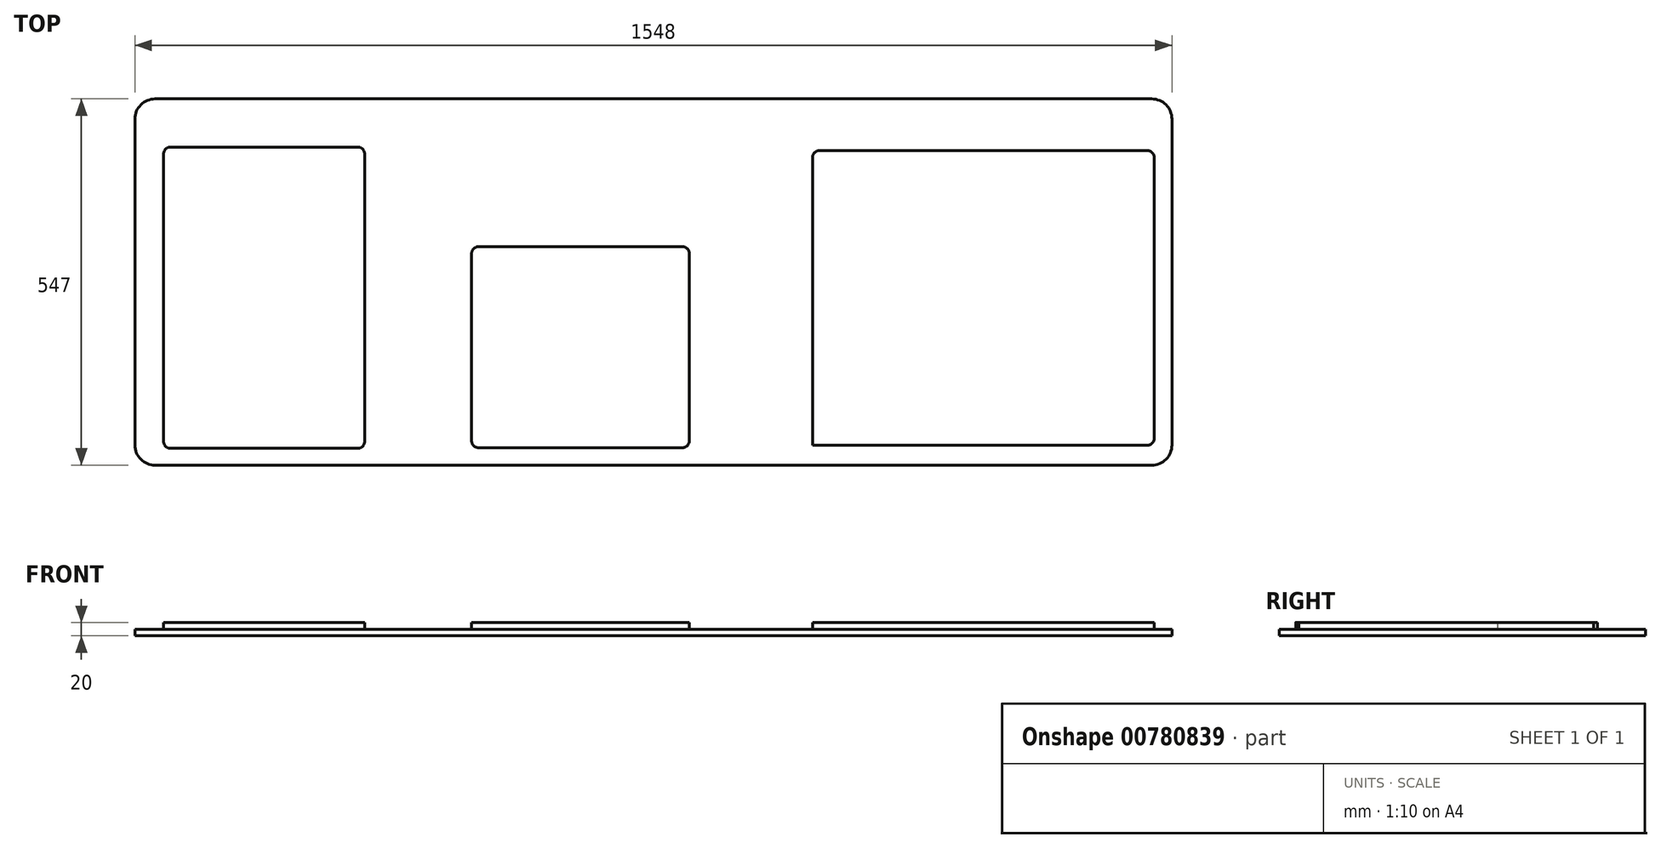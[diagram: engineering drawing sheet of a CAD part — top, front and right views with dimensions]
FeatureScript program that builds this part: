
annotation { "Feature Type Name" : "Feature", "Feature Type Description" : "" }
export const myFeature = defineFeature(function(context is Context, id is Id, definition is map)
    precondition{}
    {
        {
            var Q0;
            Q0=qCreatedBy(makeId("Top.planeOp"),FACE);
            var sketch = newSketch(context, id + "F0", { "sketchPlane" : qUnion([Q0])});
            skLineSegment(sketch, "E0.bottom", {"start": v(-744, 273.5) * mm, "end": v(744, 273.5) * mm});
            skLineSegment(sketch, "E0.top", {"start": v(-744, -273.5) * mm, "end": v(744, -273.5) * mm});
            skLineSegment(sketch, "E0.left", {"start": v(-774, 243.5) * mm, "end": v(-774, -243.5) * mm});
            skLineSegment(sketch, "E0.right", {"start": v(774, 243.5) * mm, "end": v(774, -243.5) * mm});
            skPoint(sketch, "E0.middle", {"position": v(0, 0) * mm});
            skPoint(sketch, "E1.visualSharp", {"position": v(-774, 273.5) * mm});
            skArc(sketch, "E1.filletArc", {"start": v(-744, 273.5) * mm, "mid": v(-765.21, 264.71) * mm, "end": v(-774, 243.5) * mm});
            skPoint(sketch, "E2.visualSharp", {"position": v(-774, -273.5) * mm});
            skArc(sketch, "E2.filletArc", {"start": v(-774, -243.5) * mm, "mid": v(-765.21, -264.71) * mm, "end": v(-744, -273.5) * mm});
            skPoint(sketch, "E3.visualSharp", {"position": v(774, 273.5) * mm});
            skArc(sketch, "E3.filletArc", {"start": v(774, 243.5) * mm, "mid": v(765.21, 264.71) * mm, "end": v(744, 273.5) * mm});
            skPoint(sketch, "E4.visualSharp", {"position": v(774, -273.5) * mm});
            skArc(sketch, "E4.filletArc", {"start": v(744, -273.5) * mm, "mid": v(765.21, -264.71) * mm, "end": v(774, -243.5) * mm});
            skSolve(sketch);
        }
        {
            var Q0;
            Q0=qSketchRegion(id+"F0",true);
            extrude(context, id + "F1", {"entities" : qUnion([Q0]), "oppositeDirection" : true, "depth" : 10 * mm, "offsetDistance" : 25 * mm});
        }
        {
            var Q0;
            Q0=makeQuery(id+"F1.opExtrude","CAP_FACE",FACE,{"disambiguationData":[OSD([sQuery(id+"F0.wireOp",EDGE,"E0.bottom"),sQuery(id+"F0.wireOp",EDGE,"E0.top"),sQuery(id+"F0.wireOp",EDGE,"E0.left"),sQuery(id+"F0.wireOp",EDGE,"E0.right"),sQuery(id+"F0.wireOp",EDGE,"E1.filletArc"),sQuery(id+"F0.wireOp",EDGE,"E2.filletArc"),sQuery(id+"F0.wireOp",EDGE,"E3.filletArc"),sQuery(id+"F0.wireOp",EDGE,"E4.filletArc")])],"isStart":true});
            var sketch = newSketch(context, id + "F2", { "sketchPlane" : qUnion([Q0])});
            skPoint(sketch, "E5", {"position": v(744, 0) * mm});
            skPoint(sketch, "E5.positionSnap0", {"position": v(774, 0) * mm});
            skPoint(sketch, "E6", {"position": v(598.22, -243.5) * mm});
            skLineSegment(sketch, "E7", {"start": v(237.5, 157.63) * mm, "end": v(237.5, 7.64) * mm});
            skLineSegment(sketch, "E8", {"start": v(237.5, 7.64) * mm, "end": v(237.56, -243.77) * mm});
            skPoint(sketch, "E9.orphan", {"position": v(200.21, 253.39) * mm});
            skLineSegment(sketch, "E10.bottom", {"start": v(237.56, -243.77) * mm, "end": v(737.56, -243.77) * mm});
            skLineSegment(sketch, "E10.top", {"start": v(247.56, 196.23) * mm, "end": v(737.56, 196.23) * mm});
            skLineSegment(sketch, "E10.left", {"start": v(237.56, -243.77) * mm, "end": v(237.56, 186.23) * mm});
            skLineSegment(sketch, "E10.right", {"start": v(747.56, -233.77) * mm, "end": v(747.56, 186.23) * mm});
            skPoint(sketch, "E11.visualSharp", {"position": v(237.56, 196.23) * mm});
            skArc(sketch, "E11.filletArc", {"start": v(247.56, 196.23) * mm, "mid": v(240.5, 193.3) * mm, "end": v(237.56, 186.23) * mm});
            skPoint(sketch, "E12.visualSharp", {"position": v(747.56, 196.23) * mm});
            skArc(sketch, "E12.filletArc", {"start": v(747.56, 186.23) * mm, "mid": v(744.63, 193.3) * mm, "end": v(737.56, 196.23) * mm});
            skPoint(sketch, "E13.visualSharp", {"position": v(747.56, -243.77) * mm});
            skArc(sketch, "E13.filletArc", {"start": v(737.56, -243.77) * mm, "mid": v(744.63, -240.84) * mm, "end": v(747.56, -233.77) * mm});
            skSolve(sketch);
        }
        {
            var Q0;
            Q0=makeQuery(id+"F0.imprint","IMPRINT",FACE,{"disambiguationData":[TD([[makeQuery(id+"F0.imprint","IMPRINT",EDGE,{"derivedFrom":sQuery(id+"F0.wireOp",EDGE,"E0.bottom")}),-1.0]])]});
            var sketch = newSketch(context, id + "F3", { "sketchPlane" : qUnion([Q0])});
            skLineSegment(sketch, "E14.bottom", {"start": v(-721.16, 201.52) * mm, "end": v(-441.16, 201.52) * mm});
            skLineSegment(sketch, "E14.top", {"start": v(-721.16, -248.48) * mm, "end": v(-441.16, -248.48) * mm});
            skLineSegment(sketch, "E14.left", {"start": v(-731.16, 191.52) * mm, "end": v(-731.16, -238.48) * mm});
            skLineSegment(sketch, "E14.right", {"start": v(-431.16, 191.52) * mm, "end": v(-431.16, -238.48) * mm});
            skPoint(sketch, "E15.visualSharp", {"position": v(-731.16, 201.52) * mm});
            skArc(sketch, "E15.filletArc", {"start": v(-721.16, 201.52) * mm, "mid": v(-728.23, 198.6) * mm, "end": v(-731.16, 191.52) * mm});
            skPoint(sketch, "E16.visualSharp", {"position": v(-431.16, 201.52) * mm});
            skArc(sketch, "E16.filletArc", {"start": v(-431.16, 191.52) * mm, "mid": v(-434.09, 198.6) * mm, "end": v(-441.16, 201.52) * mm});
            skPoint(sketch, "E17.visualSharp", {"position": v(-731.16, -248.48) * mm});
            skArc(sketch, "E17.filletArc", {"start": v(-731.16, -238.48) * mm, "mid": v(-728.23, -245.55) * mm, "end": v(-721.16, -248.48) * mm});
            skPoint(sketch, "E18.visualSharp", {"position": v(-431.16, -248.48) * mm});
            skArc(sketch, "E18.filletArc", {"start": v(-441.16, -248.48) * mm, "mid": v(-434.09, -245.55) * mm, "end": v(-431.16, -238.48) * mm});
            skSolve(sketch);
        }
        {
            var Q0;
            Q0=makeQuery(id+"F0.imprint","IMPRINT",FACE,{"disambiguationData":[TD([[makeQuery(id+"F0.imprint","IMPRINT",EDGE,{"derivedFrom":sQuery(id+"F0.wireOp",EDGE,"E0.bottom")}),-1.0]])]});
            var sketch = newSketch(context, id + "F4", { "sketchPlane" : qUnion([Q0])});
            skLineSegment(sketch, "E19.bottom", {"start": v(-261.35, 52.65) * mm, "end": v(43.65, 52.65) * mm});
            skLineSegment(sketch, "E19.top", {"start": v(-261.35, -247.35) * mm, "end": v(43.65, -247.35) * mm});
            skLineSegment(sketch, "E19.left", {"start": v(-271.35, 42.65) * mm, "end": v(-271.35, -237.35) * mm});
            skLineSegment(sketch, "E19.right", {"start": v(53.65, 42.65) * mm, "end": v(53.65, -237.35) * mm});
            skPoint(sketch, "E20.visualSharp", {"position": v(-271.35, 52.65) * mm});
            skArc(sketch, "E20.filletArc", {"start": v(-261.35, 52.65) * mm, "mid": v(-268.42, 49.72) * mm, "end": v(-271.35, 42.65) * mm});
            skPoint(sketch, "E21.visualSharp", {"position": v(53.65, 52.65) * mm});
            skArc(sketch, "E21.filletArc", {"start": v(53.65, 42.65) * mm, "mid": v(50.72, 49.72) * mm, "end": v(43.65, 52.65) * mm});
            skPoint(sketch, "E22.visualSharp", {"position": v(53.65, -247.35) * mm});
            skArc(sketch, "E22.filletArc", {"start": v(43.65, -247.35) * mm, "mid": v(50.72, -244.42) * mm, "end": v(53.65, -237.35) * mm});
            skPoint(sketch, "E23.visualSharp", {"position": v(-271.35, -247.35) * mm});
            skArc(sketch, "E23.filletArc", {"start": v(-271.35, -237.35) * mm, "mid": v(-268.42, -244.42) * mm, "end": v(-261.35, -247.35) * mm});
            skLineSegment(sketch, "E24", {"start": v(199.55, 274.37) * mm, "end": v(199.55, -270.7) * mm});
            skSolve(sketch);
        }
        {
            var Q0;
            Q0 = qSketchRegion(id + "F2", true);
            extrude(context, id + "F5", {"entities" : qUnion([Q0]), "operationType" : NewBodyOperationType.ADD, "depth" : 10 * mm, "offsetDistance" : 25 * mm});
        }
        {
            var Q0;
            Q0 = qSketchRegion(id + "F3", true);
            extrude(context, id + "F6", {"entities" : qUnion([Q0]), "operationType" : NewBodyOperationType.ADD, "depth" : 10 * mm, "offsetDistance" : 25 * mm});
        }
        {
            var Q0;
            Q0 = qSketchRegion(id + "F4", true);
            extrude(context, id + "F7", {"entities" : qUnion([Q0]), "operationType" : NewBodyOperationType.ADD, "depth" : 10 * mm, "offsetDistance" : 25 * mm});
        }
    });
